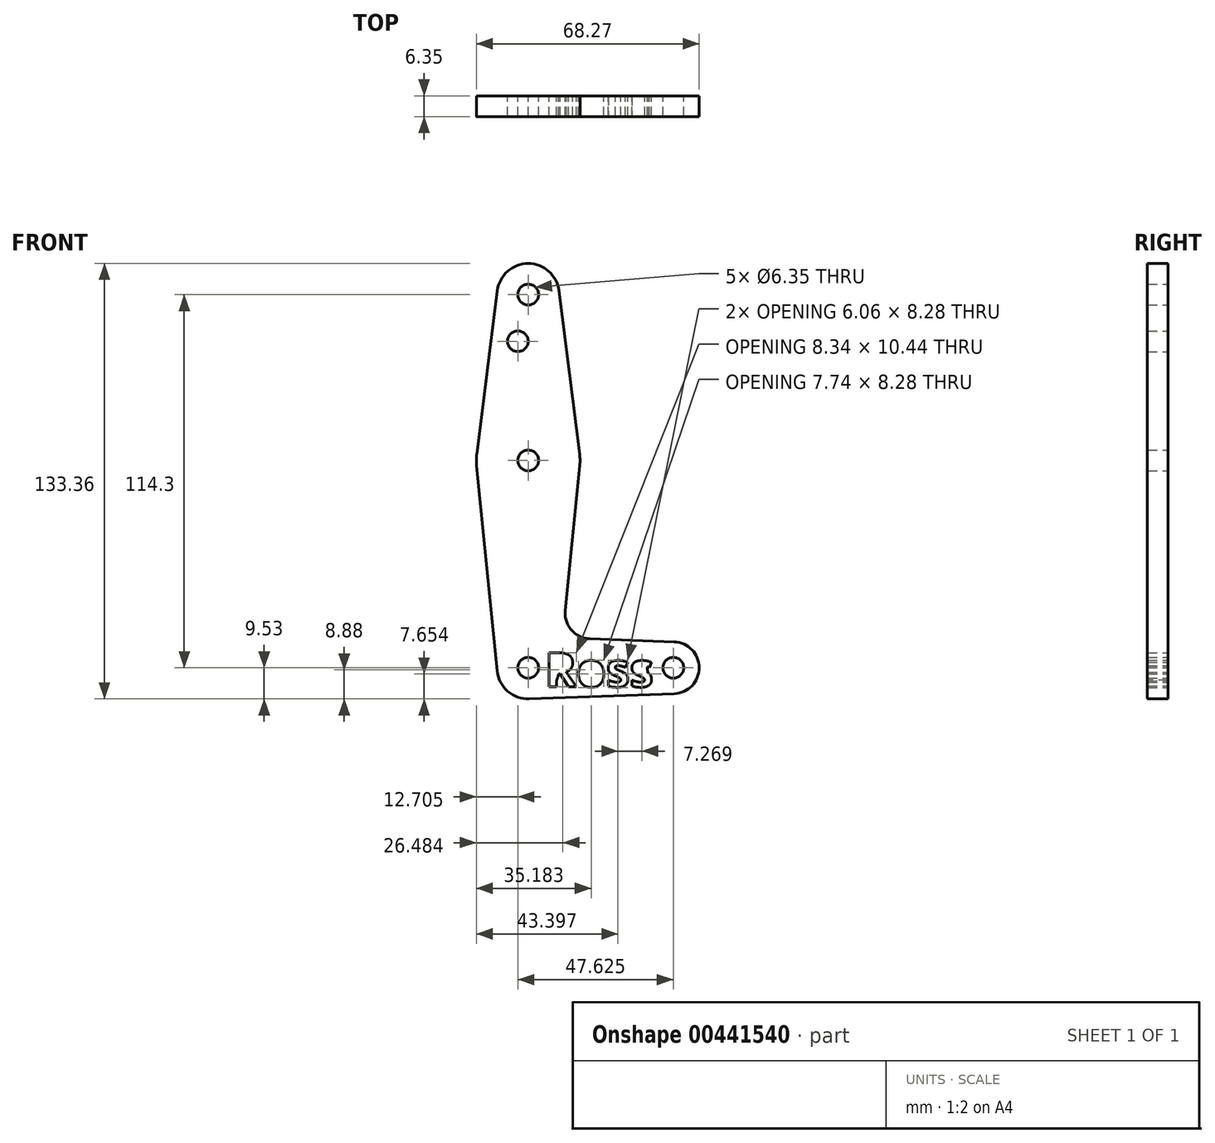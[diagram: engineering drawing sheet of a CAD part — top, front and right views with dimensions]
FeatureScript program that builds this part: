
annotation { "Feature Type Name" : "Feature", "Feature Type Description" : "" }
export const myFeature = defineFeature(function(context is Context, id is Id, definition is map)
    precondition{}
    {
        {
            var Q0;
            Q0=qCreatedBy(makeId("Front.planeOp"),FACE);
            var sketch = newSketch(context, id + "F0", { "sketchPlane" : qUnion([Q0])});
            skLineSegment(sketch, "E0", {"start": v(0, 0) * mm, "end": v(0, 114.3) * mm, "construction": true});
            skLineSegment(sketch, "E1", {"start": v(0, 0) * mm, "end": v(44.45, 0) * mm, "construction": true});
            skCircle(sketch, "E2", {"center": v(0, 114.3) * mm, "radius": 9.53 * mm});
            skCircle(sketch, "E3", {"center": v(0, 63.5) * mm, "radius": 15.88 * mm});
            skCircle(sketch, "E4", {"center": v(0, 0) * mm, "radius": 9.53 * mm});
            skCircle(sketch, "E5", {"center": v(44.45, 0) * mm, "radius": 7.94 * mm});
            skLineSegment(sketch, "E6", {"start": v(-9.45, 115.5) * mm, "end": v(-15.75, 65.48) * mm});
            skLineSegment(sketch, "E7", {"start": v(9.45, 115.5) * mm, "end": v(15.75, 65.48) * mm});
            skLineSegment(sketch, "E8", {"start": v(-15.8, 61.91) * mm, "end": v(-9.48, -0.95) * mm});
            skLineSegment(sketch, "E9", {"start": v(0.34, -9.52) * mm, "end": v(44.73, -7.93) * mm});
            skCircle(sketch, "E10", {"center": v(0, 114.3) * mm, "radius": 3.18 * mm});
            skCircle(sketch, "E11", {"center": v(0, 63.5) * mm, "radius": 3.18 * mm});
            skCircle(sketch, "E12", {"center": v(-3.18, 100.03) * mm, "radius": 3.18 * mm});
            skCircle(sketch, "E13", {"center": v(0, 0) * mm, "radius": 3.18 * mm});
            skCircle(sketch, "E14", {"center": v(44.45, 0) * mm, "radius": 3.18 * mm});
            skLineSegment(sketch, "E15", {"start": v(15.8, 61.91) * mm, "end": v(11.34, 17.6) * mm});
            skLineSegment(sketch, "E16", {"start": v(18.97, 8.85) * mm, "end": v(44.73, 7.93) * mm});
            skArc(sketch, "E17.filletArc", {"start": v(11.34, 17.6) * mm, "mid": v(13.26, 11.57) * mm, "end": v(18.97, 8.85) * mm});
            skText(sketch, "E18", { "text": "Ross", "fontName": "OpenSans-Bold.ttf"});
            const initialGuessF0  = {"E18": [0.00512, -0.00587, 1, 0, 0.01053]};
            skSetInitialGuess(sketch, initialGuessF0);
            skSolve(sketch);
        }
        {
            var Q0;
            Q0 = qSketchRegion(id + "F0", true);
            extrude(context, id + "F1", {"entities" : qUnion([Q0]), "depth" : 6.35 * mm});
        }
    });
